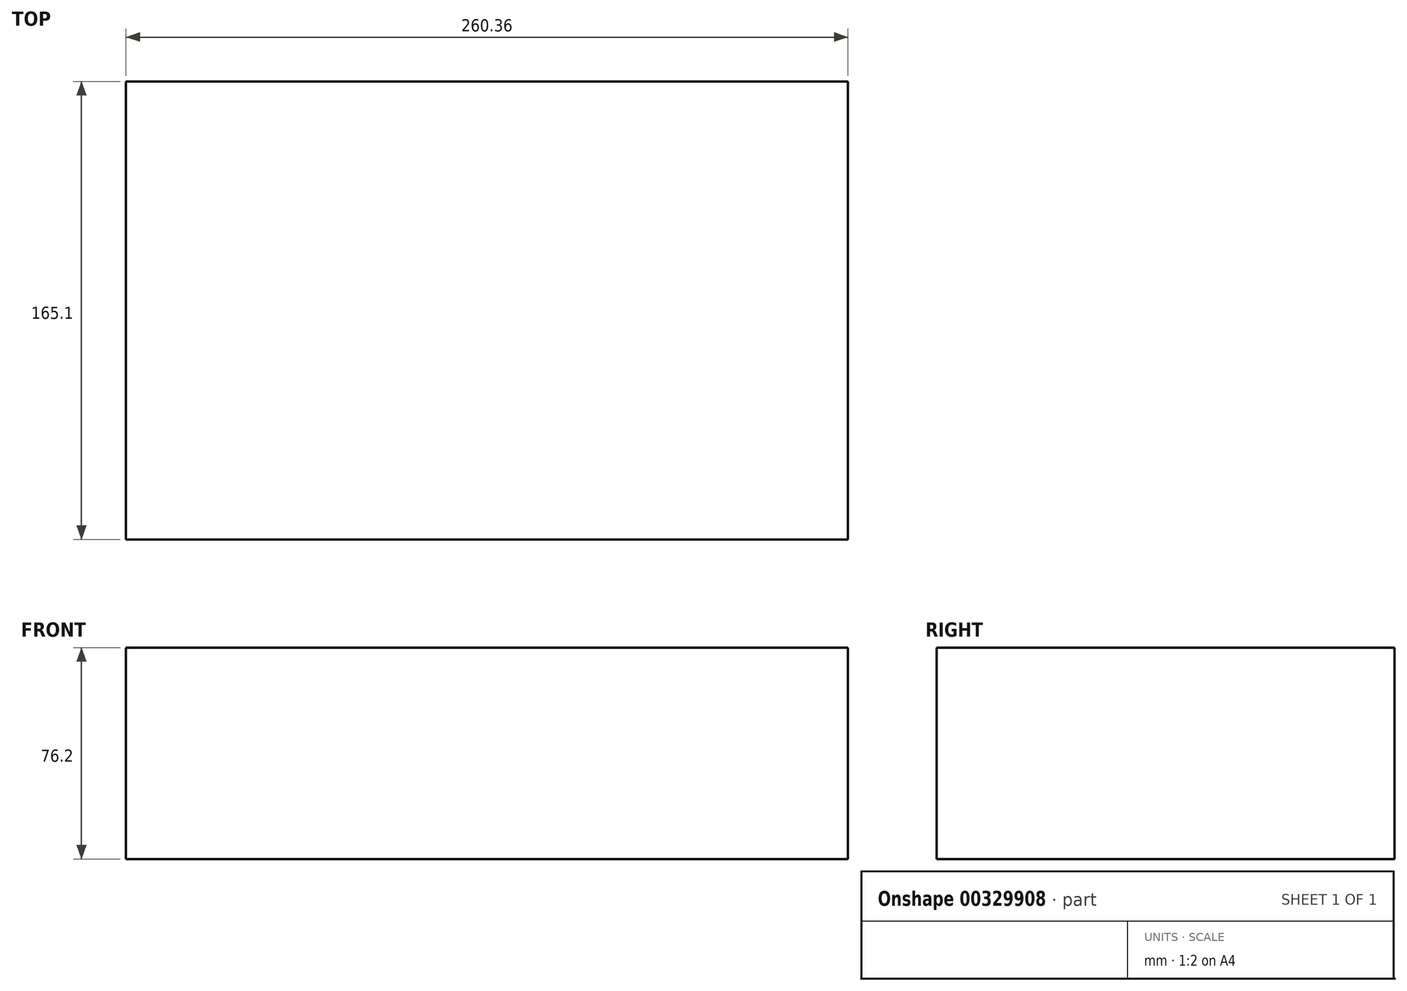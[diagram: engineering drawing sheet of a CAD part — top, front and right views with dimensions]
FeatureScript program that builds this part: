
annotation { "Feature Type Name" : "Feature", "Feature Type Description" : "" }
export const myFeature = defineFeature(function(context is Context, id is Id, definition is map)
    precondition{}
    {
        {
            var Q0;
            Q0=qCreatedBy(makeId("Top.planeOp"),FACE);
            var sketch = newSketch(context, id + "F0", { "sketchPlane" : qUnion([Q0])});
            skLineSegment(sketch, "E0.bottom", {"start": v(130.18, 82.55) * mm, "end": v(-130.18, 82.55) * mm});
            skLineSegment(sketch, "E0.top", {"start": v(130.18, -82.55) * mm, "end": v(-130.17, -82.55) * mm});
            skLineSegment(sketch, "E0.left", {"start": v(130.18, 82.55) * mm, "end": v(130.18, -82.55) * mm});
            skLineSegment(sketch, "E0.right", {"start": v(-130.18, 82.55) * mm, "end": v(-130.18, -82.55) * mm});
            skPoint(sketch, "E0.middle", {"position": v(0, 0) * mm});
            skSolve(sketch);
        }
        {
            var Q0;
            Q0 = qSketchRegion(id + "F0", true);
            extrude(context, id + "F1", {"entities" : qUnion([Q0]), "depth" : 76.2 * mm, "symmetric" : true});
        }
    });
